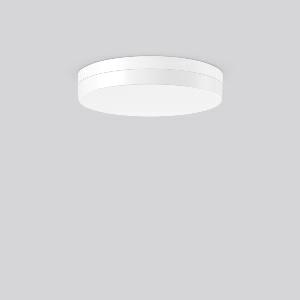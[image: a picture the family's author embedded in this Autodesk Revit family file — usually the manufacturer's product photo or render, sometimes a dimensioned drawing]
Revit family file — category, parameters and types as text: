
# Revit family: flat_slim_round_312676_002_1_19_1d78
name_source: partatom
category: Lighting Fixtures
units: mm (PartAtom-declared; Revit-internal decimal feet)

## family parameters
Cut with Voids When Loaded = No
Host = Face
Light Source = No
Part Type = Normal
Room Calculation Point = No
Round Connector Dimension = Use Diameter
Shared = No

## types (1)
- MultiLumen 1 830 (1 x LED Modul 830, 2450 lm, 3000)
    Apparent Load = 18 VA
    CIE Flux Codes = 37 67 88 84 100
    Color Rendering = 80
    Color Temperature = 3000
    Default Elevation = 1800 mm
    Height = 70 mm
    Lamp = 1 x LED Modul 830
    Lamp Light Flux = 2450 lm
    Lamp count = 1
    Length = 400 mm
    Lifetime = 50000 h
    Luminous efficacy = 136 lm/W
    Manufacturer = RZB
    ModVariant = No
    Model = 312676.002.1.19
    Mounting Place = Ceiling
    Mounting Type = Surface mounted
    Number of Poles = 1
    OnlyDefault = Yes
    Power Factor = 1
    Product Name = FLAT SLIM round
    Product group = Surface mounted ceiling and wall luminaires
    ProductGroupID = 305
    Protection Class = Protection class I
    Protection Degree = Degree of protection
    RLX_Detail_Level = 1
    RLX_Emergency_Light_Flux = 0 lm
    RLX_Emergency_Type = 0
    RLX_Emergency_Type_DB = No
    RlxData = <blob elided: 20481 chars, md5=793e497b>
    Socket = socket
    Standby Power = 0 W
    System Light Flux = 2450 lm
    System Power = 18 W
    Type Comments = MultiLumen 1 830
    Type Image = 312631.002.jpg
    URL = http://relux.com
    VarID = multilumen_1_830
    Voltage = 0 V
    Weight = 0.00 kg
    Width = 0 mm  [stored 0 ft]

note: [stored X ft] marks values corroborated as IEEE doubles in the binary element streams (Revit-internal decimal feet)

## geometry (parser evidence)
native form markers: Blend x4, Sweep x13
no freeform markers — native parametric forms only
